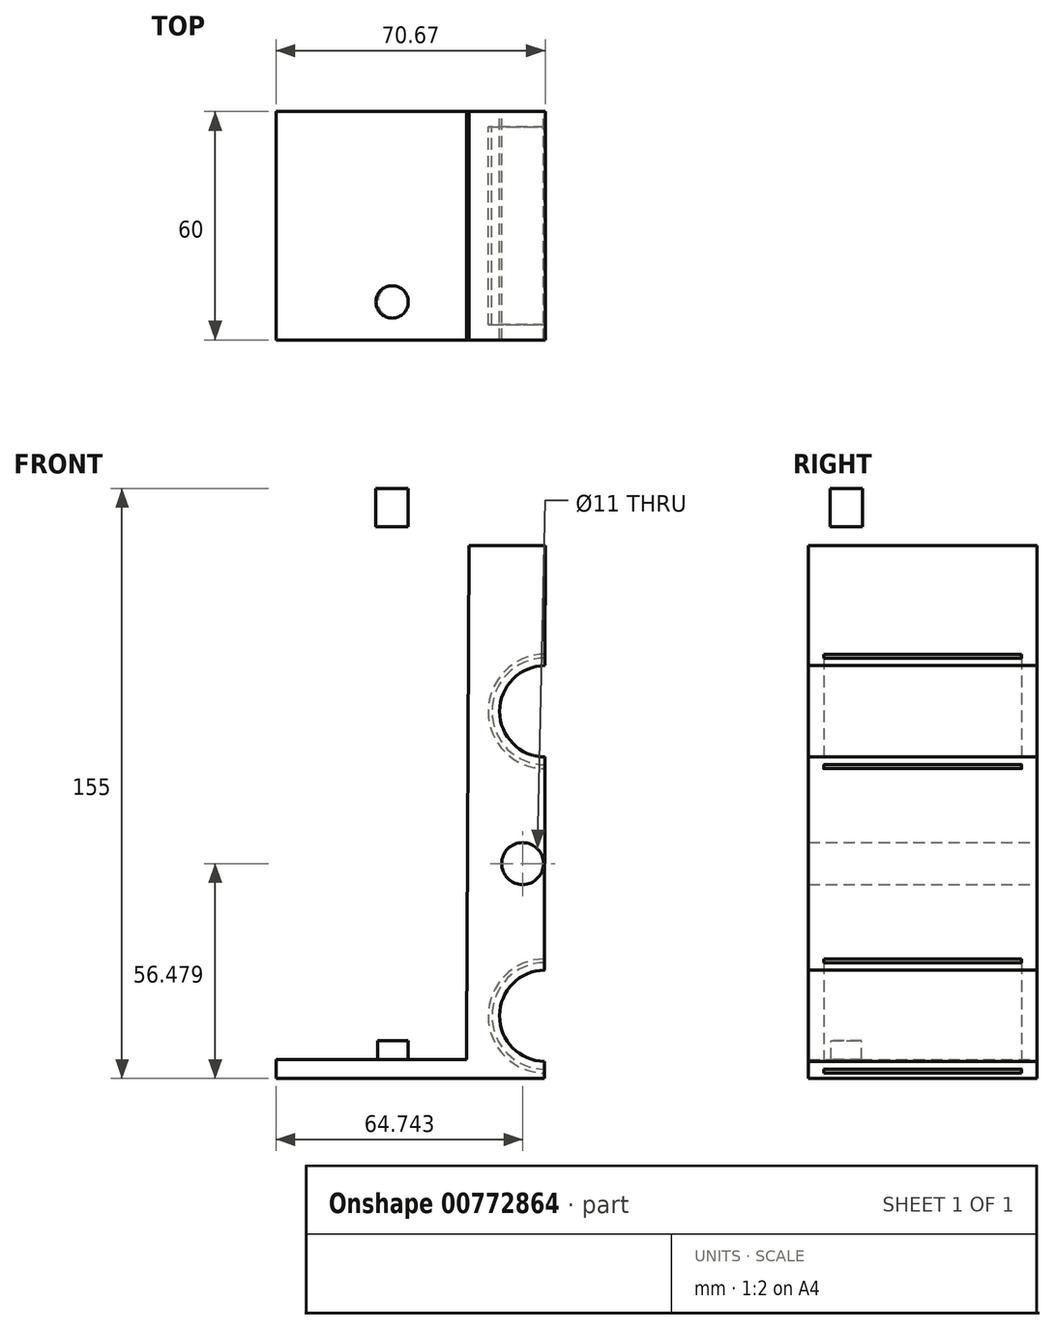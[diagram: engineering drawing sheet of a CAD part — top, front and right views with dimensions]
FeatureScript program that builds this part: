
annotation { "Feature Type Name" : "Feature", "Feature Type Description" : "" }
export const myFeature = defineFeature(function(context is Context, id is Id, definition is map)
    precondition{}
    {
        {
            var Q0;
            Q0=qCreatedBy(makeId("Front.planeOp"),FACE);
            var sketch = newSketch(context, id + "F0", { "sketchPlane" : qUnion([Q0])});
            skCircle(sketch, "E0", {"center": v(0, -41.48) * mm, "radius": 7.25 * mm});
            skCircle(sketch, "E1.MirrorC", {"center": v(0, -121.48) * mm, "radius": 7.25 * mm});
            skArc(sketch, "E2", {"start": v(0, -30.48) * mm, "mid": v(-11, -41.48) * mm, "end": v(0, -52.48) * mm});
            skArc(sketch, "E3", {"start": v(0, -29.48) * mm, "mid": v(-12, -41.48) * mm, "end": v(0, -53.48) * mm});
            skArc(sketch, "E4.MirrorCS", {"start": v(0, -133.46) * mm, "mid": v(-12, -121.46) * mm, "end": v(0, -109.46) * mm});
            skArc(sketch, "E5.MirrorCS", {"start": v(0, -132.47) * mm, "mid": v(-11, -121.47) * mm, "end": v(0, -110.47) * mm});
            skLineSegment(sketch, "E6", {"start": v(-70.04, 7.04) * mm, "end": v(-20.04, 7.04) * mm});
            skLineSegment(sketch, "E7", {"start": v(-70.7, -127.96) * mm, "end": v(-20.7, -127.96) * mm});
            skLineSegment(sketch, "E8", {"start": v(-20.04, 7.04) * mm, "end": v(-20.7, -127.96) * mm});
            skLineSegment(sketch, "E9", {"start": v(-0.2, -137.96) * mm, "end": v(0, 17.04) * mm});
            skLineSegment(sketch, "E10", {"start": v(-70.04, 7.04) * mm, "end": v(-70.04, 17.04) * mm});
            skLineSegment(sketch, "E11", {"start": v(0, 17.04) * mm, "end": v(-70.04, 17.04) * mm});
            skLineSegment(sketch, "E12", {"start": v(-70.7, -127.96) * mm, "end": v(-70.7, -137.96) * mm});
            skLineSegment(sketch, "E13", {"start": v(-0.2, -137.96) * mm, "end": v(-70.7, -137.96) * mm});
            skCircle(sketch, "E14", {"center": v(-5.95, -81.48) * mm, "radius": 5.5 * mm});
            skPoint(sketch, "E14.centerSnap0", {"position": v(-0.1, -81.48) * mm});
            skSolve(sketch);
        }
        {
            var Q0;
            Q0=makeQuery(id+"F0.imprint","IMPRINT",FACE,{"disambiguationData":[TD([[makeQuery(id+"F0.imprint","IMPRINT",EDGE,{"derivedFrom":sQuery(id+"F0.wireOp",EDGE,"E6")}),1.0]])]});
            extrude(context, id + "F1", {"entities" : qUnion([Q0]), "depth" : 60 * mm, "offsetDistance" : 25 * mm});
        }
        {
            var Q0;
            Q0=makeQuery(id+"F1.opExtrude","SWEPT_BODY",BODY,{"disambiguationData":[OSD([sQuery(id+"F0.wireOp",EDGE,"E0"),sQuery(id+"F0.wireOp",EDGE,"E1.MirrorC"),sQuery(id+"F0.wireOp",EDGE,"E6"),sQuery(id+"F0.wireOp",EDGE,"E7"),sQuery(id+"F0.wireOp",EDGE,"E8"),sQuery(id+"F0.wireOp",EDGE,"E9"),sQuery(id+"F0.wireOp",EDGE,"E10"),sQuery(id+"F0.wireOp",EDGE,"E11"),sQuery(id+"F0.wireOp",EDGE,"E12"),sQuery(id+"F0.wireOp",EDGE,"E13")])]});
            transform(context, id + "F2", {"entities" : qUnion([Q0]), "transformType" : TransformType.TRANSLATION_3D, "dx" : 0 * mm, "dy" : 30 * mm, "dz" : 0 * mm, "makeCopy" : false});
        }
        {
            var Q0;
            Q0=qCreatedBy(makeId("Front.planeOp"),FACE);
            var sketch = newSketch(context, id + "F3", { "sketchPlane" : qUnion([Q0])});
            skArc(sketch, "E15", {"start": v(0, -27.52) * mm, "mid": v(-14, -41.52) * mm, "end": v(0, -55.52) * mm});
            skArc(sketch, "E16", {"start": v(0, -26.52) * mm, "mid": v(-15, -41.52) * mm, "end": v(0, -56.52) * mm});
            skLineSegment(sketch, "E17", {"start": v(0, -56.52) * mm, "end": v(0, -55.52) * mm});
            skLineSegment(sketch, "E18", {"start": v(0, -27.52) * mm, "end": v(0, -26.52) * mm});
            skLineSegment(sketch, "E19.MirrorCS", {"start": v(0, -106.52) * mm, "end": v(0, -107.52) * mm});
            skLineSegment(sketch, "E20.MirrorCS", {"start": v(0, -135.52) * mm, "end": v(0, -136.52) * mm});
            skArc(sketch, "E21.MirrorCS", {"start": v(0, -135.52) * mm, "mid": v(-14, -121.52) * mm, "end": v(0, -107.52) * mm});
            skArc(sketch, "E22.MirrorCS", {"start": v(0, -136.52) * mm, "mid": v(-15, -121.52) * mm, "end": v(0, -106.52) * mm});
            skSolve(sketch);
        }
        {
            var Q0;
            Q0=makeQuery(id+"F3.imprint","IMPRINT",FACE,{"disambiguationData":[TD([[makeQuery(id+"F3.imprint","IMPRINT",EDGE,{"derivedFrom":sQuery(id+"F3.wireOp",EDGE,"dad4a0fd-5b9c-4c14-b859-4023bab104060.MirrorCS")}),-1.0]])]});
            var Q1;
            Q1=makeQuery(id+"F3.imprint","IMPRINT",FACE,{"disambiguationData":[TD([[makeQuery(id+"F3.imprint","IMPRINT",EDGE,{"derivedFrom":sQuery(id+"F3.wireOp",EDGE,"E15")}),-1.0]])]});
            var Q2;
            Q2=makeQuery(id+"F3.imprint","IMPRINT",FACE,{"disambiguationData":[TD([[makeQuery(id+"F3.imprint","IMPRINT",EDGE,{"derivedFrom":sQuery(id+"F3.wireOp",EDGE,"E19.MirrorCS")}),-1.0]])]});
            extrude(context, id + "F4", {"entities" : qUnion([Q0, Q1, Q2]), "operationType" : NewBodyOperationType.REMOVE, "depth" : 26 * mm, "offsetDistance" : 25 * mm, "hasSecondDirection" : true, "secondDirectionOppositeDirection" : true, "secondDirectionDepth" : 26 * mm});
        }
        {
            var Q0;
            Q0=makeQuery(id+"F1.opExtrude","SWEPT_FACE",FACE,{"disambiguationData":[OSD([sQuery(id+"F0.wireOp",EDGE,"E7")])]});
            var sketch = newSketch(context, id + "F5", { "sketchPlane" : qUnion([Q0])});
            skCircle(sketch, "E23", {"center": v(-40.04, 20) * mm, "radius": 4 * mm});
            skCircle(sketch, "E24.MirrorC", {"center": v(-40.04, -20) * mm, "radius": 4 * mm});
            skSolve(sketch);
        }
        {
            var Q0;
            Q0=makeQuery(id+"F5.imprint","IMPRINT",FACE,{"disambiguationData":[TD([[makeQuery(id+"F5.imprint","IMPRINT",EDGE,{"derivedFrom":sQuery(id+"F5.wireOp",EDGE,"E24.MirrorC")}),-1.0]])]});
            var Q1;
            Q1=makeQuery(id+"F5.imprint","IMPRINT",FACE,{"disambiguationData":[TD([[makeQuery(id+"F5.imprint","IMPRINT",EDGE,{"derivedFrom":sQuery(id+"F5.wireOp",EDGE,"E23")}),1.0]])]});
            var Q2;
            Q2=sQuery(id+"F5.wireOp",EDGE,"E23");
            var Q3;
            Q3=sQuery(id+"F5.wireOp",EDGE,"E24.MirrorC");
            extrude(context, id + "F6", {"entities" : qUnion([Q0, Q1]), "operationType" : NewBodyOperationType.REMOVE, "surfaceEntities" : qUnion([Q2, Q3]), "oppositeDirection" : true, "depth" : 5 * mm, "offsetDistance" : 25 * mm});
        }
        {
            var Q0;
            Q0=makeQuery(id+"F1.opExtrude","SWEPT_FACE",FACE,{"disambiguationData":[OSD([sQuery(id+"F0.wireOp",EDGE,"E11")])]});
            var sketch = newSketch(context, id + "F7", { "sketchPlane" : qUnion([Q0])});
            skCircle(sketch, "E25", {"center": v(-40.04, 20) * mm, "radius": 4.25 * mm});
            skCircle(sketch, "E26.MirrorC", {"center": v(-40.23, -20) * mm, "radius": 4.25 * mm});
            skSolve(sketch);
        }
        {
            var Q0;
            Q0=makeQuery(id+"F7.imprint","IMPRINT",FACE,{"disambiguationData":[TD([[makeQuery(id+"F7.imprint","IMPRINT",EDGE,{"derivedFrom":sQuery(id+"F7.wireOp",EDGE,"E25")}),1.0]])]});
            var Q1;
            Q1=makeQuery(id+"F7.imprint","IMPRINT",FACE,{"disambiguationData":[TD([[makeQuery(id+"F7.imprint","IMPRINT",EDGE,{"derivedFrom":sQuery(id+"F7.wireOp",EDGE,"E26.MirrorC")}),-1.0]])]});
            extrude(context, id + "F8", {"entities" : qUnion([Q0, Q1]), "operationType" : NewBodyOperationType.REMOVE, "oppositeDirection" : true, "depth" : 15 * mm, "offsetDistance" : 25 * mm});
        }
        {
            var Q0;
            Q0=makeQuery(id+"F1.opExtrude","SWEPT_FACE",FACE,{"disambiguationData":[OSD([sQuery(id+"F0.wireOp",EDGE,"E11")])]});
            var sketch = newSketch(context, id + "F9", { "sketchPlane" : qUnion([Q0])});
            skCircle(sketch, "E27", {"center": v(-40.14, 0) * mm, "radius": 11 * mm});
            skSolve(sketch);
        }
        {
            var Q0;
            Q0=makeQuery(id+"F9.imprint","IMPRINT",FACE,{"disambiguationData":[TD([[makeQuery(id+"F9.imprint","IMPRINT",EDGE,{"derivedFrom":sQuery(id+"F9.wireOp",EDGE,"E27")}),1.0]])]});
            extrude(context, id + "F10", {"entities" : qUnion([Q0]), "operationType" : NewBodyOperationType.REMOVE, "oppositeDirection" : true, "depth" : 25 * mm, "offsetDistance" : 25 * mm, "hasSecondDirection" : true, "secondDirectionOppositeDirection" : false, "secondDirectionDepth" : 25 * mm});
        }
    });
